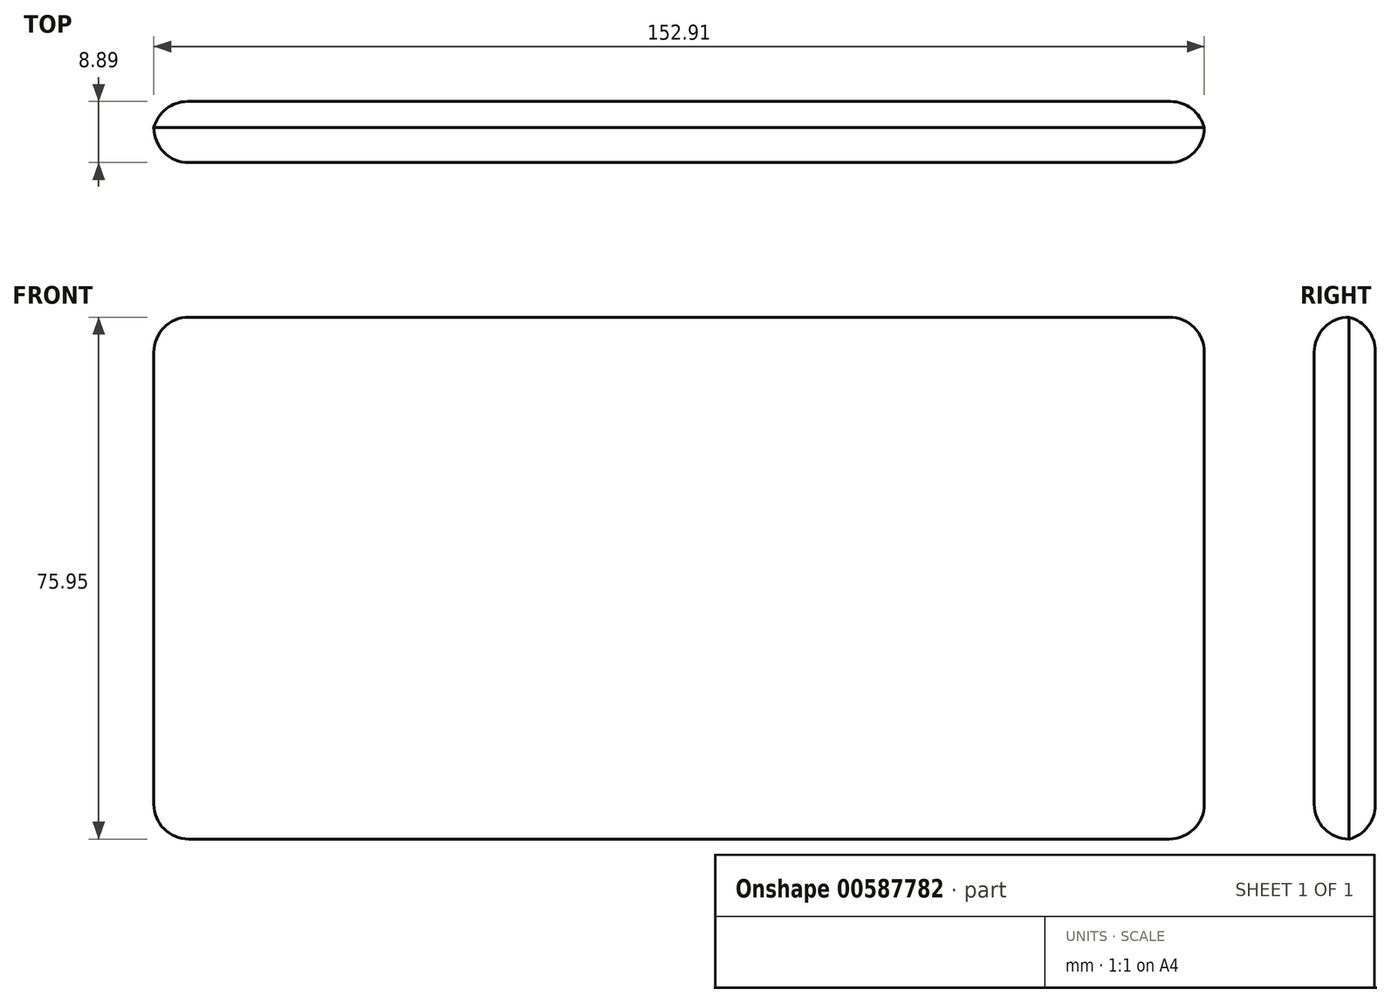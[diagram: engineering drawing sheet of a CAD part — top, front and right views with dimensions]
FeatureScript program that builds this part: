
annotation { "Feature Type Name" : "Feature", "Feature Type Description" : "" }
export const myFeature = defineFeature(function(context is Context, id is Id, definition is map)
    precondition{}
    {
        {
            var Q0;
            Q0=qCreatedBy(makeId("Front.planeOp"),FACE);
            var sketch = newSketch(context, id + "F0", { "sketchPlane" : qUnion([Q0])});
            skLineSegment(sketch, "E0.bottom", {"start": v(0, 0) * mm, "end": v(152.9, 0) * mm});
            skLineSegment(sketch, "E0.top", {"start": v(0, 75.95) * mm, "end": v(152.9, 75.95) * mm});
            skLineSegment(sketch, "E0.left", {"start": v(0, 0) * mm, "end": v(0, 75.95) * mm});
            skLineSegment(sketch, "E0.right", {"start": v(152.9, 0) * mm, "end": v(152.9, 75.95) * mm});
            skSolve(sketch);
        }
        {
            var Q0;
            Q0=makeQuery(id+"F0.imprint","IMPRINT",FACE,{"disambiguationData":[TD([[makeQuery(id+"F0.imprint","IMPRINT",EDGE,{"derivedFrom":sQuery(id+"F0.wireOp",EDGE,"E0.bottom")}),1.0]])]});
            var Q1;
            Q1 = qSketchRegion(id + "F0", true);
            extrude(context, id + "F1", {"entities" : qUnion([Q0, Q1]), "depth" : 8.9 * mm, "offsetDistance" : 25.4 * mm});
        }
        {
            var Q0;
            Q0=makeQuery(id+"F1.opExtrude","SWEPT_EDGE",EDGE,{"disambiguationData":[OSD([sQuery(id+"F0.wireOp",EDGE,"E0.top"),sQuery(id+"F0.wireOp",EDGE,"E0.right")])]});
            var Q1;
            Q1=makeQuery(id+"F1.opExtrude","SWEPT_EDGE",EDGE,{"disambiguationData":[OSD([sQuery(id+"F0.wireOp",EDGE,"E0.top"),sQuery(id+"F0.wireOp",EDGE,"E0.left")])]});
            var Q2;
            Q2=makeQuery(id+"F1.opExtrude","SWEPT_EDGE",EDGE,{"disambiguationData":[OSD([sQuery(id+"F0.wireOp",EDGE,"E0.bottom"),sQuery(id+"F0.wireOp",EDGE,"E0.right")])]});
            var Q3;
            Q3=makeQuery(id+"F1.opExtrude","SWEPT_EDGE",EDGE,{"disambiguationData":[OSD([sQuery(id+"F0.wireOp",EDGE,"E0.bottom"),sQuery(id+"F0.wireOp",EDGE,"E0.left")])]});
            fillet(context, id + "F2", {"entities" : qUnion([Q0, Q1, Q2, Q3]), "radius" : 5.08 * mm, "tangentPropagation" : true, "allowEdgeOverflow" : false});
        }
        {
            var Q0;
            Q0=makeQuery(id+"F1.opExtrude","CAP_EDGE",EDGE,{"disambiguationData":[OSD([sQuery(id+"F0.wireOp",EDGE,"E0.top")])],"isStart":false});
            fillet(context, id + "F3", {"entities" : qUnion([Q0]), "radius" : 5.08 * mm, "tangentPropagation" : true, "allowEdgeOverflow" : false});
        }
        {
            var Q0;
            Q0=makeQuery(id+"F1.opExtrude","CAP_EDGE",EDGE,{"disambiguationData":[OSD([sQuery(id+"F0.wireOp",EDGE,"E0.top")])],"isStart":true});
            fillet(context, id + "F4", {"entities" : qUnion([Q0]), "radius" : 5.08 * mm, "tangentPropagation" : true, "allowEdgeOverflow" : false});
        }
    });
